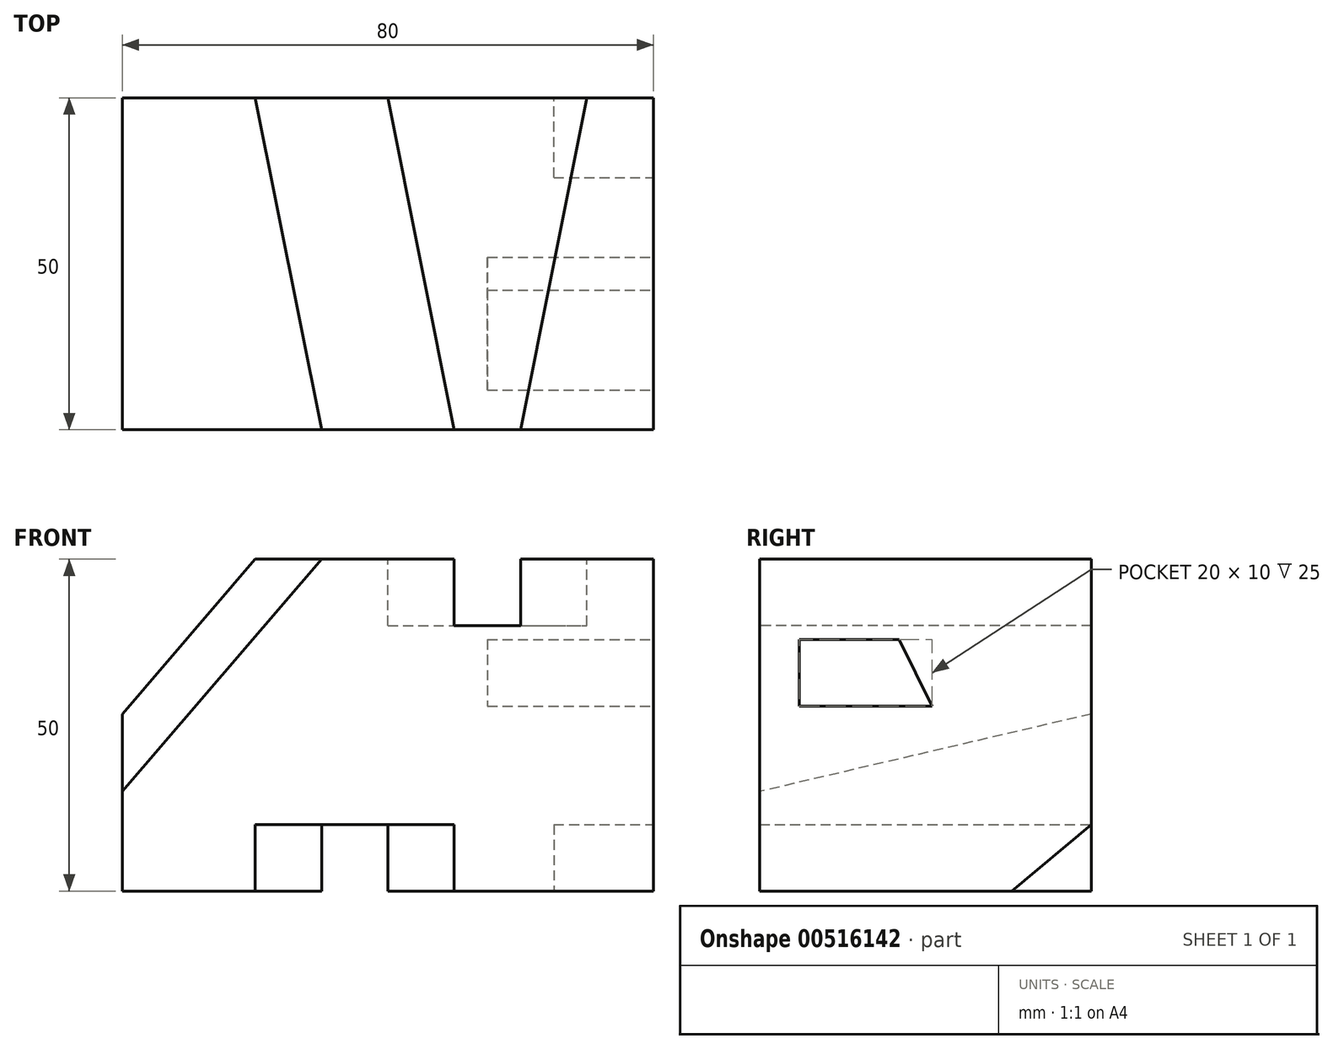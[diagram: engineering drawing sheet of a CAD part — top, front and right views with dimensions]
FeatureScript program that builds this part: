
annotation { "Feature Type Name" : "Feature", "Feature Type Description" : "" }
export const myFeature = defineFeature(function(context is Context, id is Id, definition is map)
    precondition{}
    {
        {
            var Q0;
            Q0=qCreatedBy(makeId("Top.planeOp"),FACE);
            var sketch = newSketch(context, id + "F0", { "sketchPlane" : qUnion([Q0])});
            skLineSegment(sketch, "E0.bottom", {"start": v(0, 0) * mm, "end": v(80, 0) * mm});
            skLineSegment(sketch, "E0.top", {"start": v(0, 50) * mm, "end": v(80, 50) * mm});
            skLineSegment(sketch, "E0.left", {"start": v(0, 0) * mm, "end": v(0, 50) * mm});
            skLineSegment(sketch, "E0.right", {"start": v(80, 0) * mm, "end": v(80, 50) * mm});
            skSolve(sketch);
        }
        {
            var Q0;
            Q0 = qSketchRegion(id + "F0", true);
            extrude(context, id + "F1", {"entities" : qUnion([Q0]), "depth" : 50 * mm, "offsetDistance" : 25 * mm});
        }
        {
            var Q0;
            Q0=makeQuery(id+"F1.opExtrude","CAP_FACE",FACE,{"disambiguationData":[OSD([sQuery(id+"F0.wireOp",EDGE,"E0.bottom"),sQuery(id+"F0.wireOp",EDGE,"E0.top"),sQuery(id+"F0.wireOp",EDGE,"E0.left"),sQuery(id+"F0.wireOp",EDGE,"E0.right")])],"isStart":true});
            var sketch = newSketch(context, id + "F2", { "sketchPlane" : qUnion([Q0])});
            skLineSegment(sketch, "E1", {"start": v(20, 0) * mm, "end": v(30, -50) * mm});
            skLineSegment(sketch, "E2", {"start": v(30, -50) * mm, "end": v(40, -50) * mm});
            skLineSegment(sketch, "E3", {"start": v(40, -50) * mm, "end": v(50, 0) * mm});
            skLineSegment(sketch, "E4", {"start": v(50, 0) * mm, "end": v(20, 0) * mm});
            skSolve(sketch);
        }
        {
            var Q0;
            Q0 = qSketchRegion(id + "F2", true);
            extrude(context, id + "F3", {"entities" : qUnion([Q0]), "operationType" : NewBodyOperationType.REMOVE, "oppositeDirection" : true, "depth" : 10 * mm, "offsetDistance" : 25 * mm});
        }
        {
            var Q0;
            Q0=makeQuery(id+"F1.opExtrude","SWEPT_FACE",FACE,{"disambiguationData":[OSD([sQuery(id+"F0.wireOp",EDGE,"E0.bottom")])]});
            var sketch = newSketch(context, id + "F4", { "sketchPlane" : qUnion([Q0])});
            skLineSegment(sketch, "E5", {"start": v(30, 50) * mm, "end": v(0, 15) * mm});
            skSolve(sketch);
        }
        {
            var Q0;
            Q0=makeQuery(id+"F1.opExtrude","CAP_FACE",FACE,{"disambiguationData":[OSD([sQuery(id+"F0.wireOp",EDGE,"E0.bottom"),sQuery(id+"F0.wireOp",EDGE,"E0.top"),sQuery(id+"F0.wireOp",EDGE,"E0.left"),sQuery(id+"F0.wireOp",EDGE,"E0.right")])],"isStart":false});
            var sketch = newSketch(context, id + "F5", { "sketchPlane" : qUnion([Q0])});
            skLineSegment(sketch, "E6", {"start": v(20, 50) * mm, "end": v(30, 0) * mm});
            skSolve(sketch);
        }
        {
            var Q0;
            {var subQ0=sQuery(id+"F4.wireOp",EDGE,"E5");Q0=makeQuery(id+"F4.imprint","IMPRINT",FACE,{"disambiguationData":[TD([[makeQuery(id+"F4.imprint","IMPRINT",EDGE,{"derivedFrom":subQ0}),-1.0]])]});}
            var Q1;
            Q1=sQuery(id+"F5.wireOp",EDGE,"E6");
            sweep(context, id + "F6", {"operationType" : NewBodyOperationType.REMOVE, "profiles" : qUnion([Q0]), "path" : qUnion([Q1])});
        }
        {
            var Q0;
            Q0=makeQuery(id+"F1.opExtrude","CAP_FACE",FACE,{"disambiguationData":[OSD([sQuery(id+"F0.wireOp",EDGE,"E0.bottom"),sQuery(id+"F0.wireOp",EDGE,"E0.top"),sQuery(id+"F0.wireOp",EDGE,"E0.left"),sQuery(id+"F0.wireOp",EDGE,"E0.right")])],"isStart":false});
            var sketch = newSketch(context, id + "F7", { "sketchPlane" : qUnion([Q0])});
            skLineSegment(sketch, "E7", {"start": v(40, 50) * mm, "end": v(50, 0) * mm});
            skLineSegment(sketch, "E8", {"start": v(50, 0) * mm, "end": v(60, 0) * mm});
            skLineSegment(sketch, "E9", {"start": v(60, 0) * mm, "end": v(70, 50) * mm});
            skLineSegment(sketch, "E10", {"start": v(70, 50) * mm, "end": v(40, 50) * mm});
            skSolve(sketch);
        }
        {
            var Q0;
            Q0 = qSketchRegion(id + "F7", true);
            extrude(context, id + "F8", {"entities" : qUnion([Q0]), "operationType" : NewBodyOperationType.REMOVE, "oppositeDirection" : true, "depth" : 10 * mm, "offsetDistance" : 25 * mm});
        }
        {
            var Q0;
            Q0=makeQuery(id+"F1.opExtrude","SWEPT_FACE",FACE,{"disambiguationData":[OSD([sQuery(id+"F0.wireOp",EDGE,"E0.right")])]});
            var sketch = newSketch(context, id + "F9", { "sketchPlane" : qUnion([Q0])});
            skLineSegment(sketch, "E11", {"start": v(50, 10) * mm, "end": v(38, 0) * mm});
            skSolve(sketch);
        }
        {
            var Q0;
            Q0 = qSketchRegion(id + "F9", true);
            var Q1;
            {var subQ0=sQuery(id+"F9.wireOp",EDGE,"E11");Q1=makeQuery(id+"F9.imprint","IMPRINT",FACE,{"disambiguationData":[TD([[makeQuery(id+"F9.imprint","IMPRINT",EDGE,{"derivedFrom":subQ0}),1.0]])]});}
            extrude(context, id + "F10", {"entities" : qUnion([Q0, Q1]), "operationType" : NewBodyOperationType.REMOVE, "oppositeDirection" : true, "depth" : 15 * mm, "offsetDistance" : 25 * mm});
        }
        {
            var Q0;
            Q0=makeQuery(id+"F1.opExtrude","SWEPT_FACE",FACE,{"disambiguationData":[OSD([sQuery(id+"F0.wireOp",EDGE,"E0.right")])]});
            var sketch = newSketch(context, id + "F11", { "sketchPlane" : qUnion([Q0])});
            skLineSegment(sketch, "E12", {"start": v(6, 37.87) * mm, "end": v(6, 27.87) * mm});
            skLineSegment(sketch, "E13", {"start": v(6, 27.87) * mm, "end": v(26, 27.87) * mm});
            skLineSegment(sketch, "E14", {"start": v(26, 27.87) * mm, "end": v(21, 37.87) * mm});
            skLineSegment(sketch, "E15", {"start": v(21, 37.87) * mm, "end": v(6, 37.87) * mm});
            skSolve(sketch);
        }
        {
            var Q0;
            Q0 = qSketchRegion(id + "F11", true);
            extrude(context, id + "F12", {"entities" : qUnion([Q0]), "operationType" : NewBodyOperationType.REMOVE, "oppositeDirection" : true, "depth" : 25 * mm, "offsetDistance" : 25 * mm});
        }
    });
